# Revit family: Sink-Wall_Mount-Lavatory-KOHLER-Morningside-K-12636_1
name_source: partatom
category: Plumbing Fixtures
revit_build: Autodesk Revit 2017 (Build: 20160225_1515(x64)
units: mm (PartAtom-declared; Revit-internal decimal feet)

## family parameters
Cut with Voids When Loaded = No
Host = Face
OmniClass Number = 23.31.13.00
OmniClass Title = Sinks
Part Type = Normal
Room Calculation Point = No
Round Connector Dimension = Use Diameter
Shared = No

## types (3) — shared parameters
ADA Compliant = Yes
Assembly Code = D2010400
CW Connection = No
Cold Water Inlet = Cold Water Inlet
Date Modified = 10/23/2020
Default Elevation = 36"
Drain Included = No
Finish = Kohler-Vitreous_China-0-White
HW Connection = No
Height = 7 7/16"
Hot Water Inlet = Hot Water Inlet
Length = 27"
Manufacturer = KOHLER Co.
Master Format 2014 = 22 41 16
Master Format 2014 Name = Residential Lavatories and Sinks
Material = Vitreous China
Product Documentation Link = https://www.us.kohler.com
Product Name = Morningside
Product Page URL = http://www.us.kohler.com
URL = https://www.us.kohler.com
Vent Connection = No
Waste Connection = Yes
Waste Water Outlet = Waste Water Outlet
WaterSense Certified = No
Width = 20"

## per-type parameters (varying)
| type | Description | Left Soap Dispenser Hole | Model | Right Soap Dispenser Hole | Type |
| Centerset Faucet Hole- 0 - White | 20 Inch x 27 Inch mounted/concealed arm carrier wheelchair bathroom sink with 4 Inch centerset faucet holes | No | K-12636-0 | No | 1 |
| LH Soap Dispenser Hole - 0 White | Concealed carrier arm mounted wheelchair commercial bathroom sink with 4 Inch centerset faucet holes and left-hand soap dispenser hole | Yes | K-12636-L-0 | No | 2 |
| RH Soap Dispenser Hole - 0 White | 20 Inch x 27 Inch wall-mount/concealed arm carrier wheelchair bathroom sink with 4 Inch centerset faucet holes and right-hand soap dispenser hole | No | K-12636-R-0 | Yes | 3 |

## geometry (parser evidence)
native form markers: Sweep x4
no freeform markers — native parametric forms only
